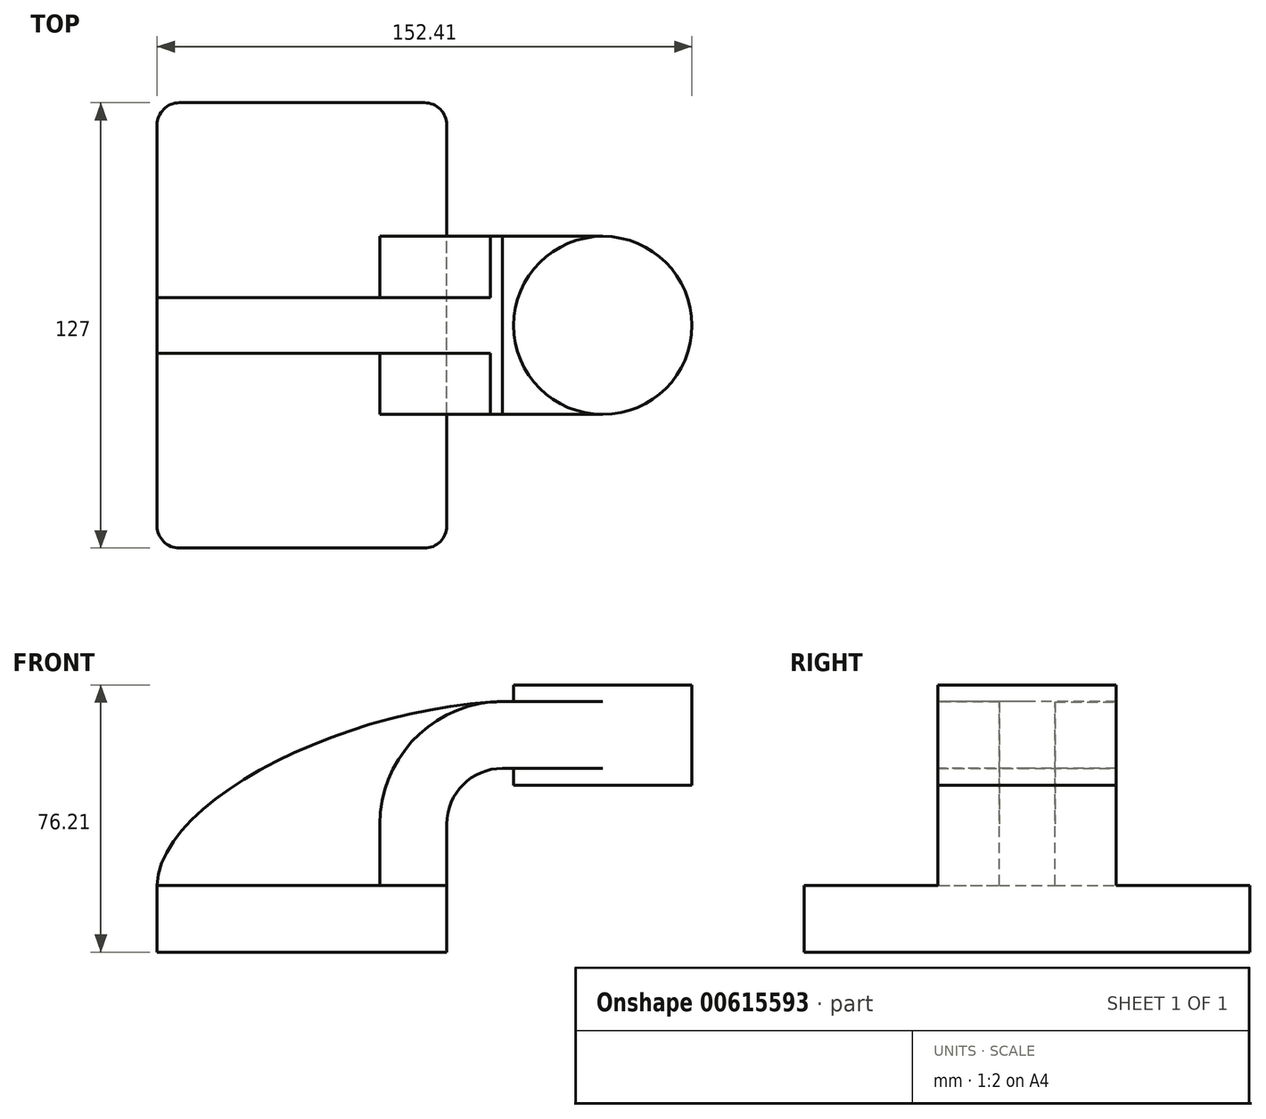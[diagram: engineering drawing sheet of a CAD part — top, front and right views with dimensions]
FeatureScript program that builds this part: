
annotation { "Feature Type Name" : "Feature", "Feature Type Description" : "" }
export const myFeature = defineFeature(function(context is Context, id is Id, definition is map)
    precondition{}
    {
        {
            var Q0;
            Q0=qCreatedBy(makeId("Front.planeOp"),FACE);
            var sketch = newSketch(context, id + "F0", { "sketchPlane" : qUnion([Q0])});
            skLineSegment(sketch, "E0.bottom", {"start": v(-41.28, 9.52) * mm, "end": v(41.27, 9.53) * mm});
            skLineSegment(sketch, "E0.top", {"start": v(-41.28, -9.53) * mm, "end": v(41.28, -9.53) * mm});
            skLineSegment(sketch, "E0.left", {"start": v(-41.28, 9.52) * mm, "end": v(-41.27, -9.53) * mm});
            skLineSegment(sketch, "E0.right", {"start": v(41.28, 9.53) * mm, "end": v(41.28, -9.52) * mm});
            skPoint(sketch, "E0.middle", {"position": v(0, 0) * mm});
            skLineSegment(sketch, "E1.bottom", {"start": v(60.33, 66.68) * mm, "end": v(111.13, 66.68) * mm});
            skLineSegment(sketch, "E1.top", {"start": v(60.33, 38.1) * mm, "end": v(111.13, 38.1) * mm});
            skLineSegment(sketch, "E1.left", {"start": v(60.33, 66.68) * mm, "end": v(60.33, 38.1) * mm});
            skLineSegment(sketch, "E1.right", {"start": v(111.13, 66.68) * mm, "end": v(111.13, 38.1) * mm});
            skPoint(sketch, "E1.middle", {"position": v(85.72, 52.39) * mm});
            skLineSegment(sketch, "E2", {"start": v(41.27, 9.53) * mm, "end": v(41.27, 27) * mm});
            skArc(sketch, "E3", {"start": v(41.27, 27) * mm, "mid": v(45.92, 38.23) * mm, "end": v(57.15, 42.88) * mm});
            skLineSegment(sketch, "E4", {"start": v(57.15, 42.88) * mm, "end": v(85.73, 42.88) * mm});
            skLineSegment(sketch, "E5.0", {"start": v(57.15, 61.93) * mm, "end": v(85.73, 61.93) * mm});
            skArc(sketch, "E5.1", {"start": v(22.23, 27) * mm, "mid": v(32.45, 51.7) * mm, "end": v(57.15, 61.93) * mm});
            skLineSegment(sketch, "E5.2", {"start": v(22.23, 9.53) * mm, "end": v(22.23, 27) * mm});
            skFitSpline(sketch, "E6", {"points": [v(-41.28, 9.53) * mm, v(57.15, 61.93) * mm], "startDerivative": vector(2.17, 73.85) * mm, "endDerivative": vector(131.53, 4.66) * mm});
            skLineSegment(sketch, "E7", {"start": v(85.73, 38.1) * mm, "end": v(85.73, 66.68) * mm});
            skSolve(sketch);
        }
        {
            var Q0;
            Q0=makeQuery(id+"F0.imprint","IMPRINT",FACE,{"disambiguationData":[TD([[makeQuery(id+"F0.imprint","IMPRINT",EDGE,{"derivedFrom":sQuery(id+"F0.wireOp",EDGE,"E0.top")}),1.0]])]});
            extrude(context, id + "F1", {"entities" : qUnion([Q0]), "endBound" : BoundingType.SYMMETRIC, "depth" : 127 * mm, "offsetDistance" : 25.4 * mm});
        }
        {
            var Q0;
            {var subQ1=sQuery(id+"F0.wireOp",EDGE,"E2");Q0=makeQuery(id+"F0.imprint","IMPRINT",FACE,{"disambiguationData":[TD([[makeQuery(id+"F0.imprint","IMPRINT",EDGE,{"derivedFrom":subQ1}),1.0]])]});}
            var Q1;
            {var subQ0=sQuery(id+"F0.wireOp",EDGE,"E5.0");var subQ1=sQuery(id+"F0.wireOp",EDGE,"E1.left");var subQ2=makeQuery(id+"F0.imprint","INTERSECT",VERTEX,{"derivedFrom":[subQ1,subQ0]});Q1=makeQuery(id+"F0.imprint","IMPRINT",FACE,{"disambiguationData":[TD([[makeQuery(id+"F0.imprint","IMPRINT",EDGE,{"disambiguationData":[TD([[subQ2,-1.0]])],"derivedFrom":subQ1}),1.0]])]});}
            extrude(context, id + "F2", {"entities" : qUnion([Q0, Q1]), "operationType" : NewBodyOperationType.ADD, "endBound" : BoundingType.SYMMETRIC, "depth" : 50.8 * mm, "offsetDistance" : 25.4 * mm});
        }
        {
            var Q0;
            {var subQ3=sQuery(id+"F0.wireOp",EDGE,"E5.2");Q0=makeQuery(id+"F0.imprint","IMPRINT",FACE,{"disambiguationData":[TD([[makeQuery(id+"F0.imprint","IMPRINT",EDGE,{"derivedFrom":subQ3}),1.0]])]});}
            extrude(context, id + "F3", {"entities" : qUnion([Q0]), "operationType" : NewBodyOperationType.ADD, "endBound" : BoundingType.SYMMETRIC, "depth" : 15.88 * mm, "offsetDistance" : 25.4 * mm});
        }
        {
            var Q0;
            {var subQ4=sQuery(id+"F0.wireOp",EDGE,"E1.right");Q0=makeQuery(id+"F0.imprint","IMPRINT",FACE,{"disambiguationData":[TD([[makeQuery(id+"F0.imprint","IMPRINT",EDGE,{"derivedFrom":subQ4}),-1.0]])]});}
            var Q1;
            Q1=sQuery(id+"F0.wireOp",EDGE,"E7");
            revolve(context, id + "F4", {"operationType" : NewBodyOperationType.ADD, "entities" : qUnion([Q0]), "axis" : qUnion([Q1]), "revolveType" : RevolveType.FULL});
        }
        {
            var Q0;
            Q0=makeQuery(id+"F1.opExtrude","CAP_EDGE",EDGE,{"disambiguationData":[OSD([sQuery(id+"F0.wireOp",EDGE,"E0.right")])],"isStart":false});
            var Q1;
            Q1=makeQuery(id+"F1.opExtrude","CAP_EDGE",EDGE,{"disambiguationData":[OSD([sQuery(id+"F0.wireOp",EDGE,"E0.right")])],"isStart":true});
            var Q2;
            Q2=makeQuery(id+"F1.opExtrude","CAP_EDGE",EDGE,{"disambiguationData":[OSD([sQuery(id+"F0.wireOp",EDGE,"E0.left")])],"isStart":true});
            var Q3;
            Q3=makeQuery(id+"F1.opExtrude","CAP_EDGE",EDGE,{"disambiguationData":[OSD([sQuery(id+"F0.wireOp",EDGE,"E0.left")])],"isStart":false});
            fillet(context, id + "F5", {"entities" : qUnion([Q0, Q1, Q2, Q3]), "radius" : 6.35 * mm, "tangentPropagation" : true, "allowEdgeOverflow" : false});
        }
    });
